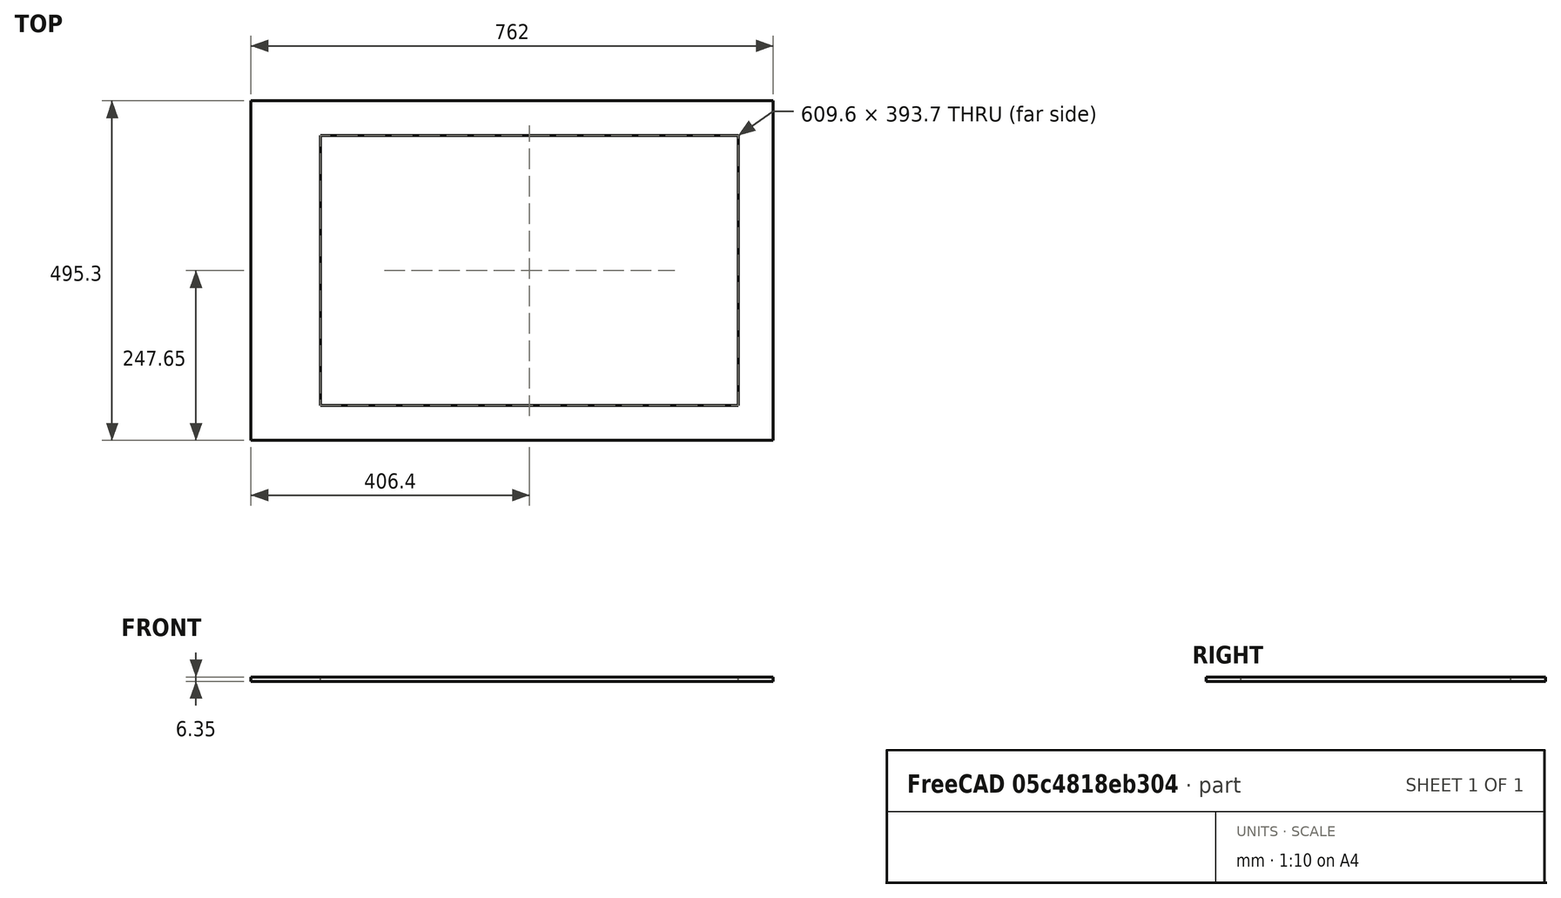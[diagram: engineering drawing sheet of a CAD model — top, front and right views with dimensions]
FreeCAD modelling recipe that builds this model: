
FCSTD DOCUMENT  (FreeCAD 0.16R6712 (Git))
Label: PC_1708_Frame_common_sides
License: CreativeCommons Attribution
LicenseURL: http://creativecommons.org/licenses/by/4.0/
objects: Sketcher::SketchObject×1, PartDesign::Pad×1
note: 3 computed .brp shape members not serialized (recipe doc carries the construction recipe); baked Part::Feature solids carry a one-line shape summary decoded from their .brp

FEATURE [Sketcher::SketchObject] Sketch
  Placement = pos=(0,0,6.35) rot=(0,0,1;0rad)
  sketch-geometry (8):
    g0: LineSegment StartX=-381 StartY=247.65 StartZ=0 EndX=381 EndY=247.65 EndZ=0
    g1: LineSegment StartX=381 StartY=247.65 StartZ=0 EndX=381 EndY=-247.65 EndZ=0
    g2: LineSegment StartX=381 StartY=-247.65 StartZ=0 EndX=-381 EndY=-247.65 EndZ=0
    g3: LineSegment StartX=-381 StartY=-247.65 StartZ=0 EndX=-381 EndY=247.65 EndZ=0
    g4: LineSegment StartX=-279.4 StartY=196.85 StartZ=0 EndX=330.2 EndY=196.85 EndZ=0
    g5: LineSegment StartX=330.2 StartY=196.85 StartZ=0 EndX=330.2 EndY=-196.85 EndZ=0
    g6: LineSegment StartX=330.2 StartY=-196.85 StartZ=0 EndX=-279.4 EndY=-196.85 EndZ=0
    g7: LineSegment StartX=-279.4 StartY=-196.85 StartZ=0 EndX=-279.4 EndY=196.85 EndZ=0
  constraints (24):
    c: Coincident(g0,g1)
    c: Coincident(g1,g2)
    c: Coincident(g2,g3)
    c: Coincident(g3,g0)
    c: Horizontal(g0)
    c: Horizontal(g2)
    c: Vertical(g1)
    c: Vertical(g3)
    c: DistanceX(g0,g0) = 762
    c: Symmetric(g1,g0,g-1)
    c: Symmetric(g0,g0,g-2)
    c: Coincident(g4,g5)
    c: Coincident(g5,g6)
    c: Coincident(g6,g7)
    c: Coincident(g7,g4)
    c: Horizontal(g4)
    c: Horizontal(g6)
    c: Vertical(g5)
    c: Vertical(g7)
    c: DistanceY(g5,g5) = 393.7
    c: Symmetric(g5,g4,g-1)
    c: DistanceX(g5,g1) = 50.8
    c: DistanceX(g2,g6) = 101.6
    c: DistanceY(g1,g1) = 495.3
FEATURE [PartDesign::Pad] Pad
  Length = 6.35
  Length2 = 100
  Placement = pos=(0,0,6.35) rot=(0,0,1;0rad)
  Sketch = -> Sketch
  Type = 0
